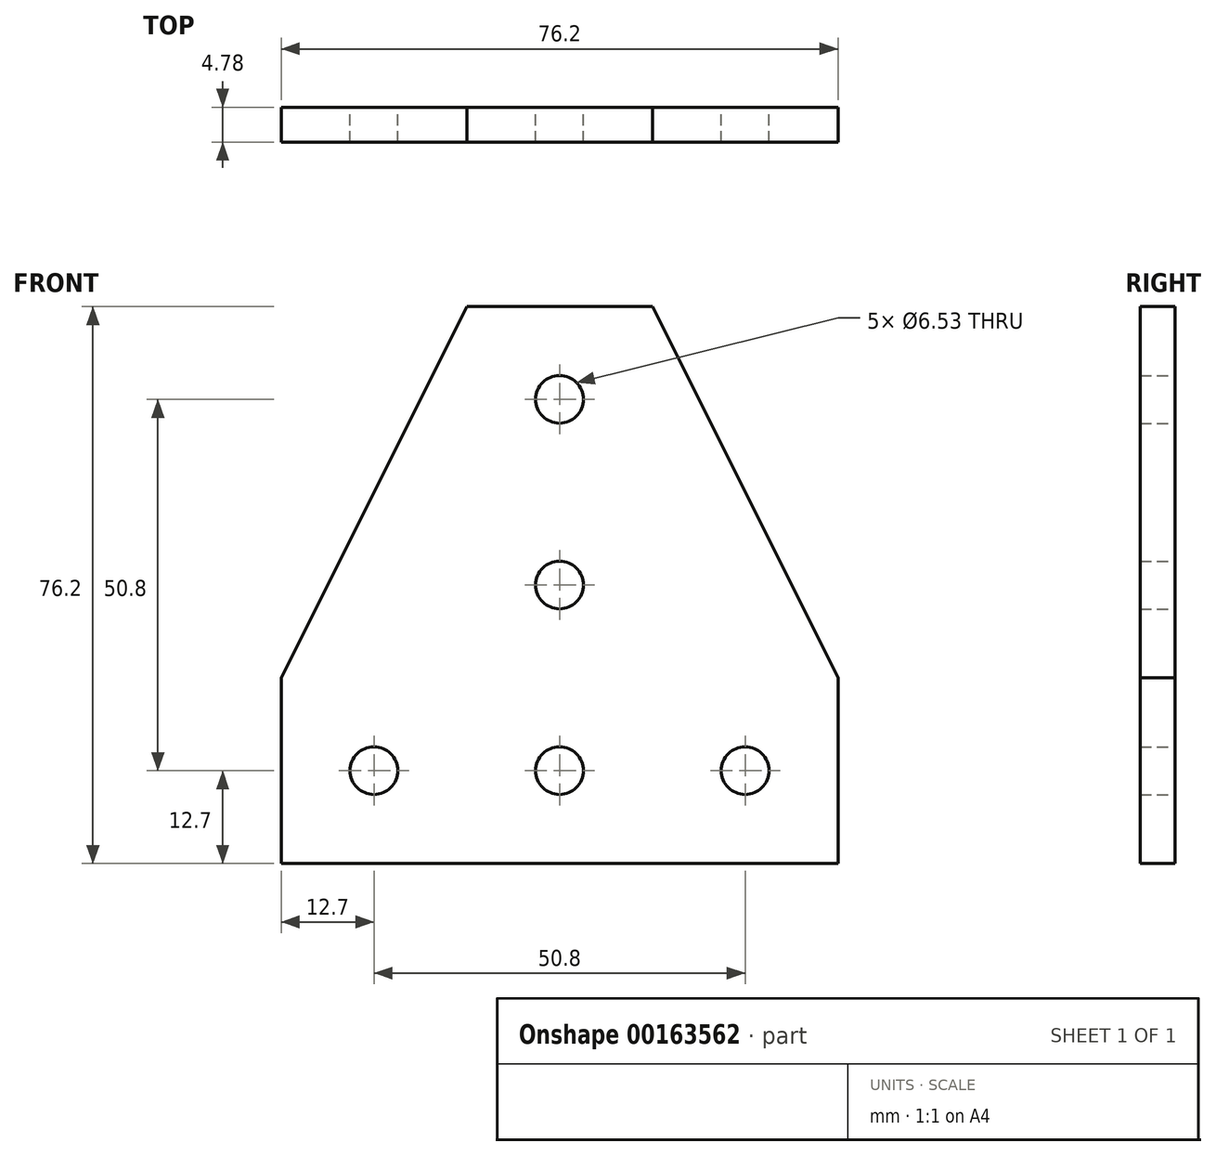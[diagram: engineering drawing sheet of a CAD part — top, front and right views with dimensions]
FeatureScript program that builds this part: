
annotation { "Feature Type Name" : "Feature", "Feature Type Description" : "" }
export const myFeature = defineFeature(function(context is Context, id is Id, definition is map)
    precondition{}
    {
        {
            var Q0;
            Q0=qCreatedBy(makeId("Front.planeOp"),FACE);
            var sketch = newSketch(context, id + "F0", { "sketchPlane" : qUnion([Q0])});
            skLineSegment(sketch, "E0.bottom", {"start": v(12.7, -38.1) * mm, "end": v(-12.7, -38.1) * mm});
            skLineSegment(sketch, "E0.top", {"start": v(12.7, 38.1) * mm, "end": v(-12.7, 38.1) * mm});
            skPoint(sketch, "E0.middle", {"position": v(0, 0) * mm});
            skLineSegment(sketch, "E1", {"start": v(0, -38.1) * mm, "end": v(0, -25.4) * mm, "construction": true});
            skPoint(sketch, "E1.endSnap0", {"position": v(0, -38.1) * mm});
            skLineSegment(sketch, "E2.bottom", {"start": v(38.1, -38.1) * mm, "end": v(-38.1, -38.1) * mm});
            skLineSegment(sketch, "E2.left", {"start": v(38.1, -38.1) * mm, "end": v(38.1, -12.7) * mm});
            skLineSegment(sketch, "E2.right", {"start": v(-38.1, -38.1) * mm, "end": v(-38.1, -12.7) * mm});
            skPoint(sketch, "E2.middle", {"position": v(0, -25.4) * mm});
            skLineSegment(sketch, "E3", {"start": v(-38.1, -12.7) * mm, "end": v(-12.7, 38.1) * mm});
            skLineSegment(sketch, "E4", {"start": v(12.7, 38.1) * mm, "end": v(38.1, -12.7) * mm});
            skCircle(sketch, "E5", {"center": v(0, -25.4) * mm, "radius": 3.26 * mm});
            skLineSegment(sketch, "E6", {"start": v(0, -25.4) * mm, "end": v(25.4, -25.4) * mm, "construction": true});
            skCircle(sketch, "E7", {"center": v(25.4, -25.4) * mm, "radius": 3.26 * mm});
            skCircle(sketch, "E8.MirrorC", {"center": v(-25.4, -25.4) * mm, "radius": 3.26 * mm});
            skLineSegment(sketch, "E9", {"start": v(0, -25.4) * mm, "end": v(0, 25.4) * mm, "construction": true});
            skCircle(sketch, "E10", {"center": v(0, 25.4) * mm, "radius": 3.26 * mm});
            skCircle(sketch, "E11", {"center": v(0, 0) * mm, "radius": 3.26 * mm});
            skSolve(sketch);
        }
        {
            var Q0;
            Q0=makeQuery(id+"F0.imprint","IMPRINT",FACE,{"disambiguationData":[TD([[makeQuery(id+"F0.imprint","IMPRINT",EDGE,{"derivedFrom":sQuery(id+"F0.wireOp",EDGE,"E0.top")}),1.0]])]});
            extrude(context, id + "F1", {"entities" : qUnion([Q0]), "depth" : 4.78 * mm});
        }
    });
